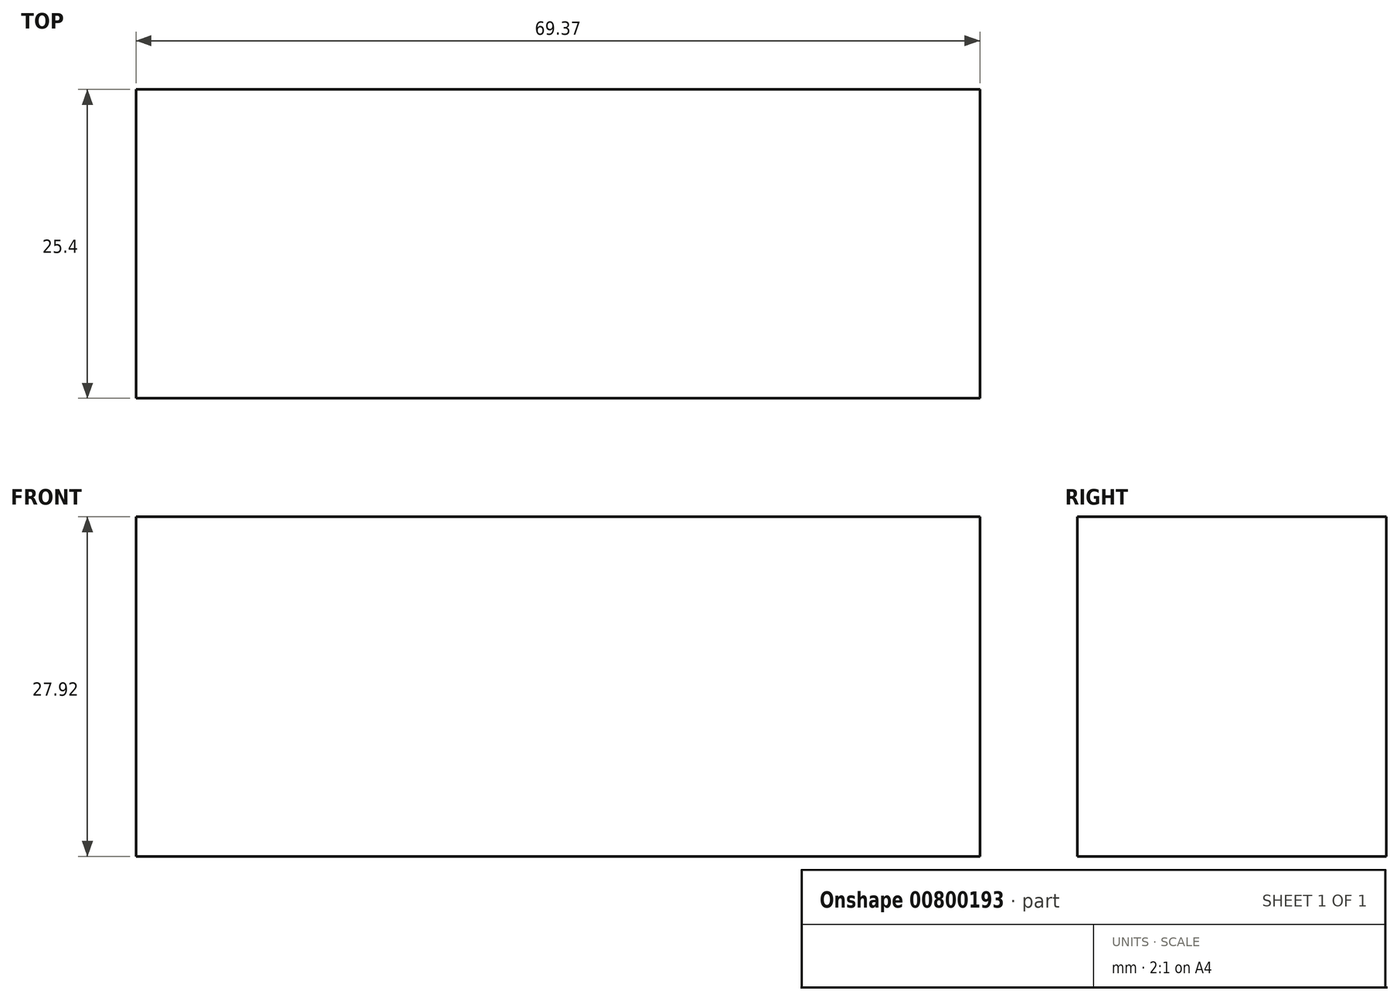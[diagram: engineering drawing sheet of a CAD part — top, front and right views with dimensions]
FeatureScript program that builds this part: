
annotation { "Feature Type Name" : "Feature", "Feature Type Description" : "" }
export const myFeature = defineFeature(function(context is Context, id is Id, definition is map)
    precondition{}
    {
        {
            var Q0;
            Q0=qCreatedBy(makeId("Front.planeOp"),FACE);
            var sketch = newSketch(context, id + "F0", { "sketchPlane" : qUnion([Q0])});
            skLineSegment(sketch, "E0.bottom", {"start": v(-86.49, 45.62) * mm, "end": v(-17.12, 45.62) * mm});
            skLineSegment(sketch, "E0.top", {"start": v(-86.49, 17.7) * mm, "end": v(-17.12, 17.7) * mm});
            skLineSegment(sketch, "E0.left", {"start": v(-86.49, 45.62) * mm, "end": v(-86.49, 17.7) * mm});
            skLineSegment(sketch, "E0.right", {"start": v(-17.12, 45.62) * mm, "end": v(-17.12, 17.7) * mm});
            skSolve(sketch);
        }
        {
            var Q0;
            Q0=makeQuery(id+"F0.imprint","IMPRINT",FACE,{"disambiguationData":[TD([[makeQuery(id+"F0.imprint","IMPRINT",EDGE,{"derivedFrom":sQuery(id+"F0.wireOp",EDGE,"E0.bottom")}),-1.0]])]});
            extrude(context, id + "F1", {"entities" : qUnion([Q0]), "depth" : 25.4 * mm, "offsetDistance" : 25.4 * mm});
        }
    });
